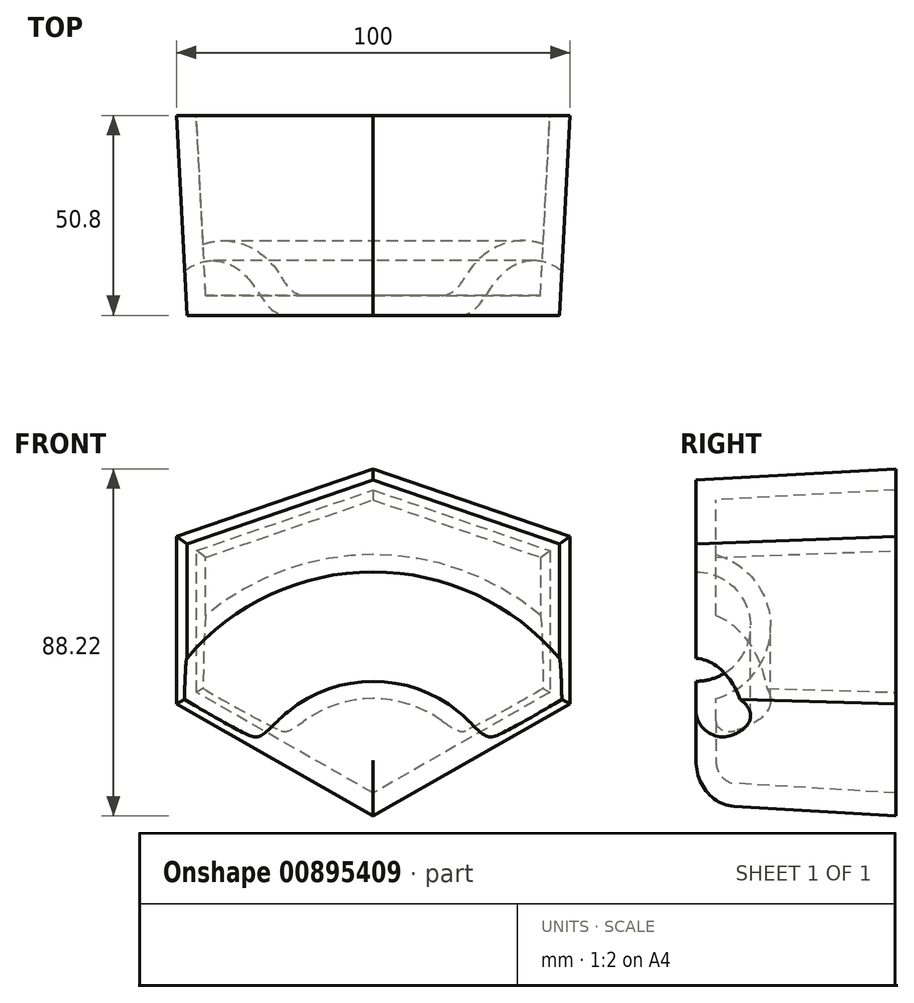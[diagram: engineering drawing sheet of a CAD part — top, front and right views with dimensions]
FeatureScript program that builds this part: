
annotation { "Feature Type Name" : "Feature", "Feature Type Description" : "" }
export const myFeature = defineFeature(function(context is Context, id is Id, definition is map)
    precondition{}
    {
        {
            var Q0;
            Q0=qCreatedBy(makeId("Front.planeOp"),FACE);
            var sketch = newSketch(context, id + "F0", { "sketchPlane" : qUnion([Q0])});
            skLineSegment(sketch, "E0", {"start": v(0, 0) * mm, "end": v(0, 94.07) * mm, "construction": true});
            skLineSegment(sketch, "E1", {"start": v(0, 88.22) * mm, "end": v(50, 71.06) * mm});
            skLineSegment(sketch, "E2", {"start": v(50, 71.06) * mm, "end": v(50, 28.49) * mm});
            skLineSegment(sketch, "E3", {"start": v(50, 28.49) * mm, "end": v(0, 0) * mm});
            skLineSegment(sketch, "E4.MirrorCS", {"start": v(0, 88.22) * mm, "end": v(-50, 71.06) * mm});
            skLineSegment(sketch, "E5.MirrorCS", {"start": v(-50, 28.49) * mm, "end": v(0, 0) * mm});
            skLineSegment(sketch, "E6.MirrorCS", {"start": v(-50, 71.06) * mm, "end": v(-50, 28.49) * mm});
            skSolve(sketch);
        }
        {
            var Q0;
            Q0 = qSketchRegion(id + "F0", true);
            extrude(context, id + "F1", {"entities" : qUnion([Q0]), "depth" : 50.8 * mm, "offsetDistance" : 25.4 * mm, "hasDraft" : true, "draftAngle" : 3 * degree, "draftPullDirection" : true});
        }
        {
            var Q0;
            Q0=qCreatedBy(makeId("Right.planeOp"),FACE);
            var sketch = newSketch(context, id + "F2", { "sketchPlane" : qUnion([Q0])});
            skCircle(sketch, "E7", {"center": v(-50.8, 48.14) * mm, "radius": 13.9 * mm});
            skLineSegment(sketch, "E8", {"start": v(0, 0) * mm, "end": v(-69.03, 0) * mm, "construction": true});
            skSolve(sketch);
        }
        {
            var Q0;
            Q0 = qSketchRegion(id + "F2", true);
            var Q1;
            Q1=sQuery(id+"F2.wireOp",EDGE,"E8");
            revolve(context, id + "F3", {"operationType" : NewBodyOperationType.REMOVE, "surfaceOperationType" : NewSurfaceOperationType.NEW, "entities" : qUnion([Q0]), "axis" : qUnion([Q1]), "revolveType" : RevolveType.FULL, "oppositeDirection" : true});
        }
        {
            var Q0;
            Q0=makeQuery(id+"F1.opExtrude","CAP_EDGE",EDGE,{"disambiguationData":[OSD([sQuery(id+"F0.wireOp",EDGE,"E3")])],"isStart":false});
            var Q1;
            Q1=makeQuery(id+"F1.opExtrude","CAP_EDGE",EDGE,{"disambiguationData":[OSD([sQuery(id+"F0.wireOp",EDGE,"E5.MirrorCS")])],"isStart":false});
            fillet(context, id + "F4", {"entities" : qUnion([Q0, Q1]), "radius" : 10.16 * mm, "tangentPropagation" : true, "allowEdgeOverflow" : false});
        }
        {
            var Q0;
            Q0=makeQuery(id+"F1.opExtrude","CAP_FACE",FACE,{"disambiguationData":[OSD([sQuery(id+"F0.wireOp",EDGE,"E1"),sQuery(id+"F0.wireOp",EDGE,"E2"),sQuery(id+"F0.wireOp",EDGE,"E3"),sQuery(id+"F0.wireOp",EDGE,"E4.MirrorCS"),sQuery(id+"F0.wireOp",EDGE,"E5.MirrorCS"),sQuery(id+"F0.wireOp",EDGE,"E6.MirrorCS")])],"isStart":true});
            shell(context, id + "F5", {"entities" : qUnion([Q0]), "thickness" : 5.08 * mm});
        }
    });
